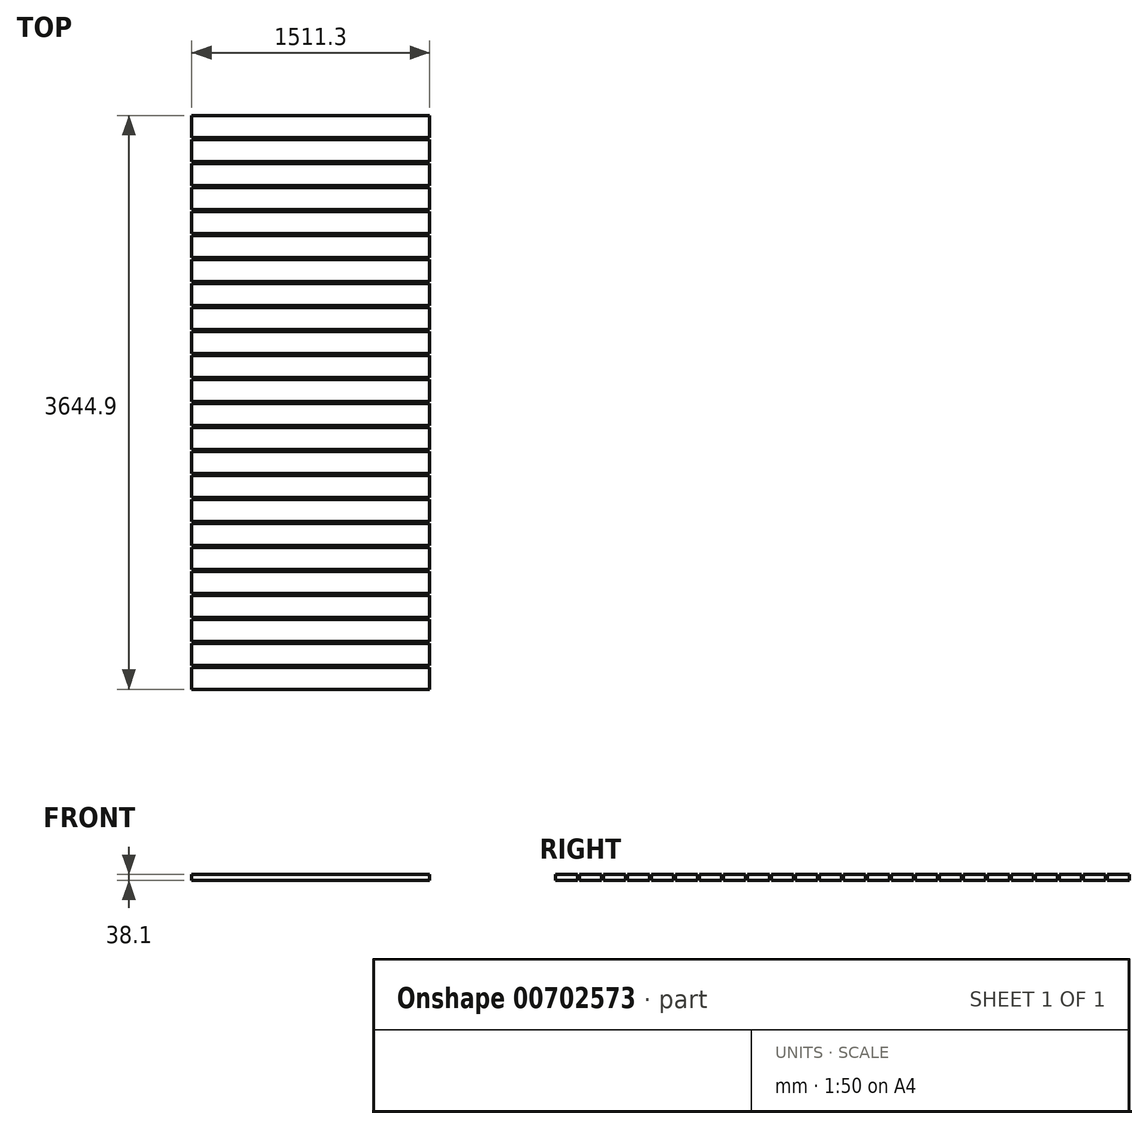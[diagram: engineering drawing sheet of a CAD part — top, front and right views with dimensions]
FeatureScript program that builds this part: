
annotation { "Feature Type Name" : "Feature", "Feature Type Description" : "" }
export const myFeature = defineFeature(function(context is Context, id is Id, definition is map)
    precondition{}
    {
        {
            var Q0;
            Q0=qCreatedBy(makeId("Top.planeOp"),FACE);
            var sketch = newSketch(context, id + "F0", { "sketchPlane" : qUnion([Q0])});
            skLineSegment(sketch, "E0.bottom", {"start": v(571.34, -616.83) * mm, "end": v(-939.96, -616.83) * mm});
            skLineSegment(sketch, "E1", {"start": v(-939.96, -616.83) * mm, "end": v(-939.96, -477.13) * mm});
            skLineSegment(sketch, "E2", {"start": v(-939.96, -477.13) * mm, "end": v(571.34, -477.13) * mm});
            skLineSegment(sketch, "E3", {"start": v(571.34, -616.83) * mm, "end": v(571.34, -477.13) * mm});
            skLineSegment(sketch, "E4.bottom", {"start": v(-939.96, -464.43) * mm, "end": v(571.34, -464.43) * mm});
            skLineSegment(sketch, "E4.top", {"start": v(-939.96, -324.73) * mm, "end": v(571.34, -324.73) * mm});
            skLineSegment(sketch, "E4.left", {"start": v(-939.96, -464.43) * mm, "end": v(-939.96, -324.73) * mm});
            skLineSegment(sketch, "E4.right", {"start": v(571.34, -464.43) * mm, "end": v(571.34, -324.73) * mm});
            skLineSegment(sketch, "E5.bottom", {"start": v(571.34, -312.03) * mm, "end": v(-939.96, -312.03) * mm});
            skLineSegment(sketch, "E5.top", {"start": v(571.34, -172.33) * mm, "end": v(-939.96, -172.33) * mm});
            skLineSegment(sketch, "E5.left", {"start": v(571.34, -312.03) * mm, "end": v(571.34, -172.33) * mm});
            skLineSegment(sketch, "E5.right", {"start": v(-939.96, -312.03) * mm, "end": v(-939.96, -172.33) * mm});
            skLineSegment(sketch, "E6.bottom", {"start": v(-939.96, -159.63) * mm, "end": v(571.34, -159.63) * mm});
            skLineSegment(sketch, "E6.top", {"start": v(-939.96, -19.93) * mm, "end": v(571.34, -19.93) * mm});
            skLineSegment(sketch, "E6.left", {"start": v(-939.96, -159.63) * mm, "end": v(-939.96, -19.93) * mm});
            skLineSegment(sketch, "E6.right", {"start": v(571.34, -159.63) * mm, "end": v(571.34, -19.93) * mm});
            skLineSegment(sketch, "E7.bottom", {"start": v(571.34, -7.23) * mm, "end": v(-939.96, -7.23) * mm});
            skLineSegment(sketch, "E7.top", {"start": v(571.34, 132.47) * mm, "end": v(-939.96, 132.47) * mm});
            skLineSegment(sketch, "E7.left", {"start": v(571.34, -7.23) * mm, "end": v(571.34, 132.47) * mm});
            skLineSegment(sketch, "E7.right", {"start": v(-939.96, -7.23) * mm, "end": v(-939.96, 132.47) * mm});
            skLineSegment(sketch, "E8.bottom", {"start": v(-939.96, 145.17) * mm, "end": v(571.34, 145.17) * mm});
            skLineSegment(sketch, "E8.top", {"start": v(-939.96, 284.87) * mm, "end": v(571.34, 284.87) * mm});
            skLineSegment(sketch, "E8.left", {"start": v(-939.96, 145.17) * mm, "end": v(-939.96, 284.87) * mm});
            skLineSegment(sketch, "E8.right", {"start": v(571.34, 145.17) * mm, "end": v(571.34, 284.87) * mm});
            skLineSegment(sketch, "E9.bottom", {"start": v(571.34, 297.57) * mm, "end": v(-939.96, 297.57) * mm});
            skLineSegment(sketch, "E9.top", {"start": v(571.34, 437.27) * mm, "end": v(-939.96, 437.27) * mm});
            skLineSegment(sketch, "E9.left", {"start": v(571.34, 297.57) * mm, "end": v(571.34, 437.27) * mm});
            skLineSegment(sketch, "E9.right", {"start": v(-939.96, 297.57) * mm, "end": v(-939.96, 437.27) * mm});
            skLineSegment(sketch, "E10.bottom", {"start": v(571.34, 449.97) * mm, "end": v(-939.96, 449.97) * mm});
            skLineSegment(sketch, "E11", {"start": v(-939.96, 449.97) * mm, "end": v(-939.96, 589.67) * mm});
            skLineSegment(sketch, "E12", {"start": v(-939.96, 589.67) * mm, "end": v(571.34, 589.67) * mm});
            skLineSegment(sketch, "E13", {"start": v(571.34, 449.97) * mm, "end": v(571.34, 589.67) * mm});
            skLineSegment(sketch, "E14.bottom", {"start": v(-939.96, 602.37) * mm, "end": v(571.34, 602.37) * mm});
            skLineSegment(sketch, "E14.top", {"start": v(-939.96, 742.07) * mm, "end": v(571.34, 742.07) * mm});
            skLineSegment(sketch, "E14.left", {"start": v(-939.96, 602.37) * mm, "end": v(-939.96, 742.07) * mm});
            skLineSegment(sketch, "E14.right", {"start": v(571.34, 602.37) * mm, "end": v(571.34, 742.07) * mm});
            skLineSegment(sketch, "E15.bottom", {"start": v(571.34, 754.77) * mm, "end": v(-939.96, 754.77) * mm});
            skLineSegment(sketch, "E15.top", {"start": v(571.34, 894.47) * mm, "end": v(-939.96, 894.47) * mm});
            skLineSegment(sketch, "E15.left", {"start": v(571.34, 754.77) * mm, "end": v(571.34, 894.47) * mm});
            skLineSegment(sketch, "E15.right", {"start": v(-939.96, 754.77) * mm, "end": v(-939.96, 894.47) * mm});
            skLineSegment(sketch, "E16.bottom", {"start": v(-939.96, 907.17) * mm, "end": v(571.34, 907.17) * mm});
            skLineSegment(sketch, "E16.top", {"start": v(-939.96, 1046.87) * mm, "end": v(571.34, 1046.87) * mm});
            skLineSegment(sketch, "E16.left", {"start": v(-939.96, 907.17) * mm, "end": v(-939.96, 1046.87) * mm});
            skLineSegment(sketch, "E16.right", {"start": v(571.34, 907.17) * mm, "end": v(571.34, 1046.87) * mm});
            skLineSegment(sketch, "E17.bottom", {"start": v(571.34, 1059.57) * mm, "end": v(-939.96, 1059.57) * mm});
            skLineSegment(sketch, "E17.top", {"start": v(571.34, 1199.27) * mm, "end": v(-939.96, 1199.27) * mm});
            skLineSegment(sketch, "E17.left", {"start": v(571.34, 1059.57) * mm, "end": v(571.34, 1199.27) * mm});
            skLineSegment(sketch, "E17.right", {"start": v(-939.96, 1059.57) * mm, "end": v(-939.96, 1199.27) * mm});
            skLineSegment(sketch, "E18.bottom", {"start": v(-939.96, 1211.97) * mm, "end": v(571.34, 1211.97) * mm});
            skLineSegment(sketch, "E18.top", {"start": v(-939.96, 1351.67) * mm, "end": v(571.34, 1351.67) * mm});
            skLineSegment(sketch, "E18.left", {"start": v(-939.96, 1211.97) * mm, "end": v(-939.96, 1351.67) * mm});
            skLineSegment(sketch, "E18.right", {"start": v(571.34, 1211.97) * mm, "end": v(571.34, 1351.67) * mm});
            skLineSegment(sketch, "E19.bottom", {"start": v(571.34, 1364.37) * mm, "end": v(-939.96, 1364.37) * mm});
            skLineSegment(sketch, "E19.top", {"start": v(571.34, 1504.07) * mm, "end": v(-939.96, 1504.07) * mm});
            skLineSegment(sketch, "E19.left", {"start": v(571.34, 1364.37) * mm, "end": v(571.34, 1504.07) * mm});
            skLineSegment(sketch, "E19.right", {"start": v(-939.96, 1364.37) * mm, "end": v(-939.96, 1504.07) * mm});
            skLineSegment(sketch, "E20.bottom", {"start": v(571.34, 1516.77) * mm, "end": v(-939.96, 1516.77) * mm});
            skLineSegment(sketch, "E21", {"start": v(-939.96, 1516.77) * mm, "end": v(-939.96, 1656.47) * mm});
            skLineSegment(sketch, "E22", {"start": v(-939.96, 1656.47) * mm, "end": v(571.34, 1656.47) * mm});
            skLineSegment(sketch, "E23", {"start": v(571.34, 1516.77) * mm, "end": v(571.34, 1656.47) * mm});
            skLineSegment(sketch, "E24.bottom", {"start": v(-939.96, 1669.17) * mm, "end": v(571.34, 1669.17) * mm});
            skLineSegment(sketch, "E24.top", {"start": v(-939.96, 1808.87) * mm, "end": v(571.34, 1808.87) * mm});
            skLineSegment(sketch, "E24.left", {"start": v(-939.96, 1669.17) * mm, "end": v(-939.96, 1808.87) * mm});
            skLineSegment(sketch, "E24.right", {"start": v(571.34, 1669.17) * mm, "end": v(571.34, 1808.87) * mm});
            skLineSegment(sketch, "E25.bottom", {"start": v(571.34, 1821.57) * mm, "end": v(-939.96, 1821.57) * mm});
            skLineSegment(sketch, "E25.top", {"start": v(571.34, 1961.27) * mm, "end": v(-939.96, 1961.27) * mm});
            skLineSegment(sketch, "E25.left", {"start": v(571.34, 1821.57) * mm, "end": v(571.34, 1961.27) * mm});
            skLineSegment(sketch, "E25.right", {"start": v(-939.96, 1821.57) * mm, "end": v(-939.96, 1961.27) * mm});
            skLineSegment(sketch, "E26.bottom", {"start": v(-939.96, 1973.97) * mm, "end": v(571.34, 1973.97) * mm});
            skLineSegment(sketch, "E26.top", {"start": v(-939.96, 2113.67) * mm, "end": v(571.34, 2113.67) * mm});
            skLineSegment(sketch, "E26.left", {"start": v(-939.96, 1973.97) * mm, "end": v(-939.96, 2113.67) * mm});
            skLineSegment(sketch, "E26.right", {"start": v(571.34, 1973.97) * mm, "end": v(571.34, 2113.67) * mm});
            skLineSegment(sketch, "E27.bottom", {"start": v(571.34, 2126.37) * mm, "end": v(-939.96, 2126.37) * mm});
            skLineSegment(sketch, "E27.top", {"start": v(571.34, 2266.07) * mm, "end": v(-939.96, 2266.07) * mm});
            skLineSegment(sketch, "E27.left", {"start": v(571.34, 2126.37) * mm, "end": v(571.34, 2266.07) * mm});
            skLineSegment(sketch, "E27.right", {"start": v(-939.96, 2126.37) * mm, "end": v(-939.96, 2266.07) * mm});
            skLineSegment(sketch, "E28.bottom", {"start": v(-939.96, 2278.77) * mm, "end": v(571.34, 2278.77) * mm});
            skLineSegment(sketch, "E28.top", {"start": v(-939.96, 2418.47) * mm, "end": v(571.34, 2418.47) * mm});
            skLineSegment(sketch, "E28.left", {"start": v(-939.96, 2278.77) * mm, "end": v(-939.96, 2418.47) * mm});
            skLineSegment(sketch, "E28.right", {"start": v(571.34, 2278.77) * mm, "end": v(571.34, 2418.47) * mm});
            skLineSegment(sketch, "E29.bottom", {"start": v(571.34, 2431.17) * mm, "end": v(-939.96, 2431.17) * mm});
            skLineSegment(sketch, "E29.top", {"start": v(571.34, 2570.87) * mm, "end": v(-939.96, 2570.87) * mm});
            skLineSegment(sketch, "E29.left", {"start": v(571.34, 2431.17) * mm, "end": v(571.34, 2570.87) * mm});
            skLineSegment(sketch, "E29.right", {"start": v(-939.96, 2431.17) * mm, "end": v(-939.96, 2570.87) * mm});
            skLineSegment(sketch, "E30.bottom", {"start": v(571.34, 2583.57) * mm, "end": v(-939.96, 2583.57) * mm});
            skLineSegment(sketch, "E31", {"start": v(-939.96, 2583.57) * mm, "end": v(-939.96, 2723.27) * mm});
            skLineSegment(sketch, "E32", {"start": v(-939.96, 2723.27) * mm, "end": v(571.34, 2723.27) * mm});
            skLineSegment(sketch, "E33", {"start": v(571.34, 2583.57) * mm, "end": v(571.34, 2723.27) * mm});
            skLineSegment(sketch, "E34.bottom", {"start": v(-939.96, 2735.97) * mm, "end": v(571.34, 2735.97) * mm});
            skLineSegment(sketch, "E34.top", {"start": v(-939.96, 2875.67) * mm, "end": v(571.34, 2875.67) * mm});
            skLineSegment(sketch, "E34.left", {"start": v(-939.96, 2735.97) * mm, "end": v(-939.96, 2875.67) * mm});
            skLineSegment(sketch, "E34.right", {"start": v(571.34, 2735.97) * mm, "end": v(571.34, 2875.67) * mm});
            skLineSegment(sketch, "E35.bottom", {"start": v(571.34, 2888.37) * mm, "end": v(-939.96, 2888.37) * mm});
            skLineSegment(sketch, "E35.top", {"start": v(571.34, 3028.07) * mm, "end": v(-939.96, 3028.07) * mm});
            skLineSegment(sketch, "E35.left", {"start": v(571.34, 2888.37) * mm, "end": v(571.34, 3028.07) * mm});
            skLineSegment(sketch, "E35.right", {"start": v(-939.96, 2888.37) * mm, "end": v(-939.96, 3028.07) * mm});
            skSolve(sketch);
        }
        {
            var Q0;
            Q0=qSketchRegion(id+"F0",true);
            extrude(context, id + "F1", {"entities" : qUnion([Q0]), "depth" : 38.1 * mm, "offsetDistance" : 25.4 * mm});
        }
    });
